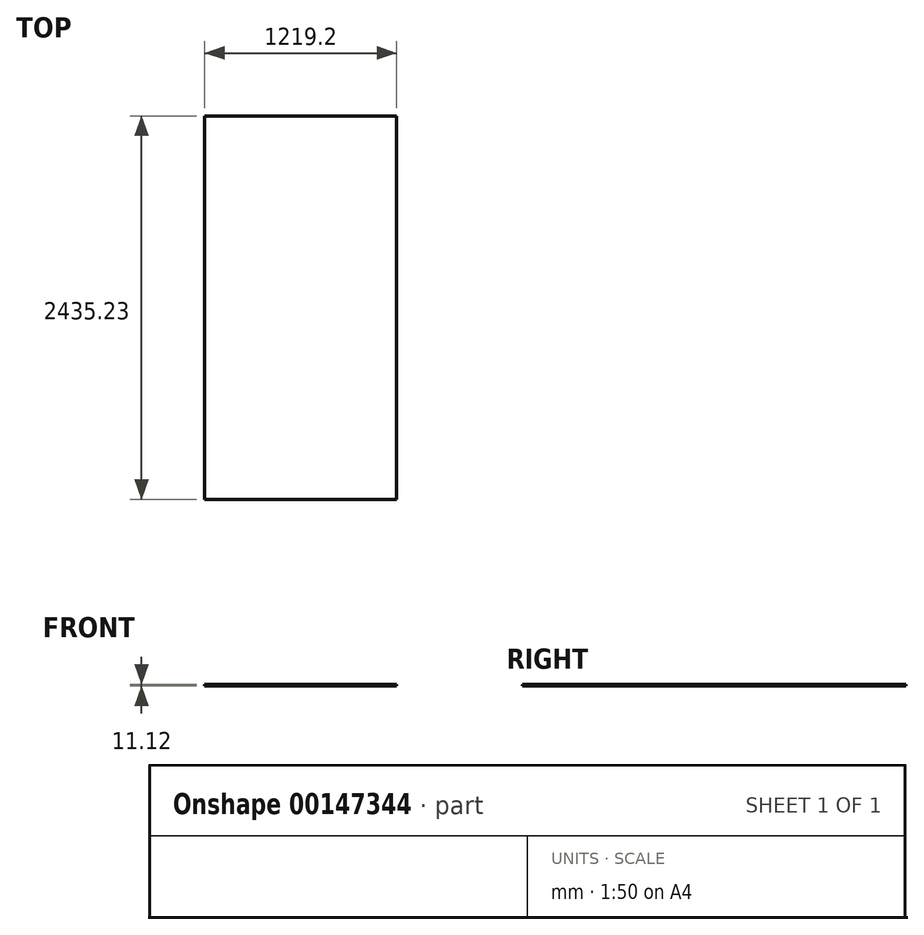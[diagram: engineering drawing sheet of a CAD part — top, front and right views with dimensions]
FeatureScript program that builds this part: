
annotation { "Feature Type Name" : "Feature", "Feature Type Description" : "" }
export const myFeature = defineFeature(function(context is Context, id is Id, definition is map)
    precondition{}
    {
        {
            var Q0;
            Q0=qCreatedBy(makeId("Top.planeOp"),FACE);
            var sketch = newSketch(context, id + "F0", { "sketchPlane" : qUnion([Q0])});
            skLineSegment(sketch, "E0.bottom", {"start": v(-609.6, 1911.45) * mm, "end": v(609.6, 1911.45) * mm});
            skLineSegment(sketch, "E0.top", {"start": v(-609.6, -523.78) * mm, "end": v(609.6, -523.78) * mm});
            skLineSegment(sketch, "E0.left", {"start": v(-609.6, 1911.45) * mm, "end": v(-609.6, -523.78) * mm});
            skLineSegment(sketch, "E0.right", {"start": v(609.6, 1911.45) * mm, "end": v(609.6, -523.78) * mm});
            skSolve(sketch);
        }
        {
            var Q0;
            Q0=qSketchRegion(id+"F0",true);
            extrude(context, id + "F1", {"entities" : qUnion([Q0]), "endBound" : BoundingType.SYMMETRIC, "depth" : 11.1 * mm});
        }
    });
